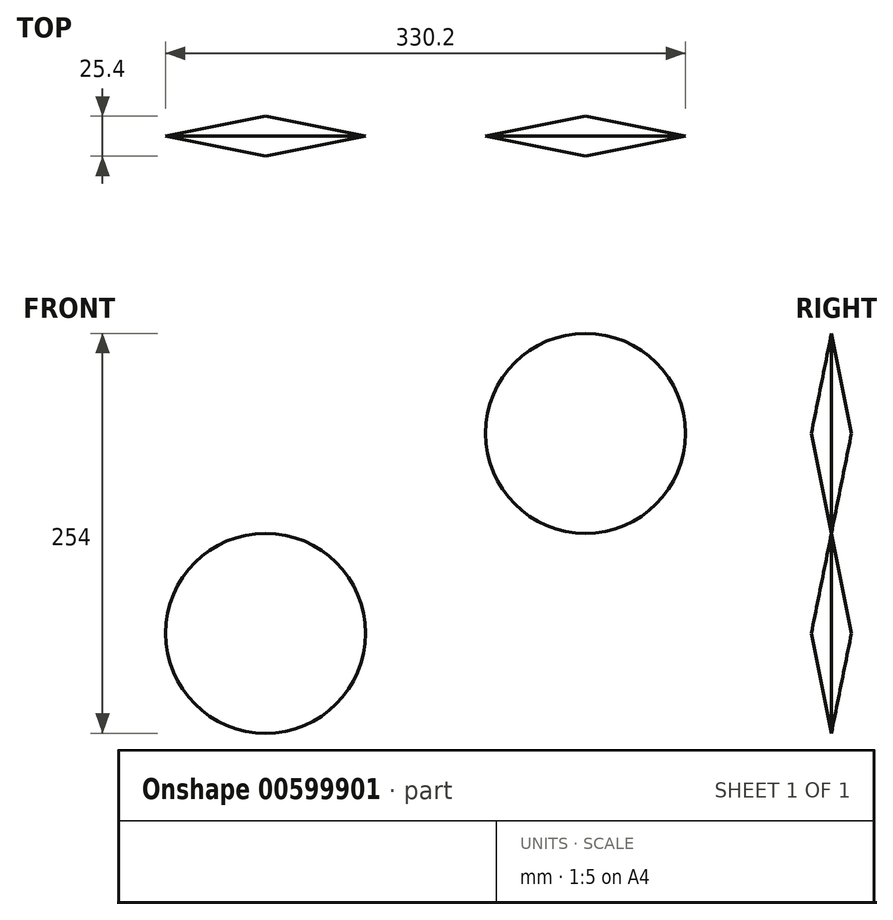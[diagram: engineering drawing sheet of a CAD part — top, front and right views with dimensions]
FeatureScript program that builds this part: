
annotation { "Feature Type Name" : "Feature", "Feature Type Description" : "" }
export const myFeature = defineFeature(function(context is Context, id is Id, definition is map)
    precondition{}
    {
        {
            var Q0;
            Q0=qCreatedBy(makeId("Front.planeOp"),FACE);
            var sketch = newSketch(context, id + "F0", { "sketchPlane" : qUnion([Q0])});
            skCircle(sketch, "E0", {"center": v(0, 0) * mm, "radius": 63.5 * mm});
            skSolve(sketch);
        }
        {
            var Q0;
            Q0 = qSketchRegion(id + "F0", true);
            extrude(context, id + "F1", {"entities" : qUnion([Q0]), "depth" : 25.4 * mm, "offsetDistance" : 25.4 * mm});
        }
        {
            var Q0;
            Q0=qCreatedBy(makeId("Top.planeOp"),FACE);
            var sketch = newSketch(context, id + "F2", { "sketchPlane" : qUnion([Q0])});
            skLineSegment(sketch, "E1", {"start": v(63.5, 0) * mm, "end": v(63.5, -25.4) * mm});
            skLineSegment(sketch, "E2.0", {"start": v(63.5, -25.4) * mm, "end": v(-63.5, -25.4) * mm});
            skLineSegment(sketch, "E3.0", {"start": v(63.5, 0) * mm, "end": v(-63.5, 0) * mm});
            skLineSegment(sketch, "E4", {"start": v(63.5, -12.7) * mm, "end": v(0, -25.4) * mm});
            skLineSegment(sketch, "E5", {"start": v(0, -25.4) * mm, "end": v(63.5, -25.4) * mm});
            skLineSegment(sketch, "E6", {"start": v(63.5, -12.7) * mm, "end": v(0, 0) * mm});
            skLineSegment(sketch, "E7", {"start": v(0, 0) * mm, "end": v(63.5, 0) * mm});
            skSolve(sketch);
        }
        {
            var Q0;
            Q0=qCreatedBy(makeId("Top.planeOp"),FACE);
            var sketch = newSketch(context, id + "F3", { "sketchPlane" : qUnion([Q0])});
            skLineSegment(sketch, "E8", {"start": v(0, 0) * mm, "end": v(0, 42.85) * mm});
            skSolve(sketch);
        }
        {
            var Q0;
            {var subQ2=sQuery(id+"F2.wireOp",EDGE,"E4");Q0=makeQuery(id+"F2.imprint","IMPRINT",FACE,{"disambiguationData":[TD([[makeQuery(id+"F2.imprint","IMPRINT",EDGE,{"derivedFrom":subQ2}),1.0]])]});}
            var Q1;
            {var subQ2=sQuery(id+"F2.wireOp",EDGE,"E6");Q1=makeQuery(id+"F2.imprint","IMPRINT",FACE,{"disambiguationData":[TD([[makeQuery(id+"F2.imprint","IMPRINT",EDGE,{"derivedFrom":subQ2}),-1.0]])]});}
            var Q2;
            Q2=sQuery(id+"F3.wireOp",EDGE,"E8");
            revolve(context, id + "F4", {"operationType" : NewBodyOperationType.REMOVE, "entities" : qUnion([Q0, Q1]), "axis" : qUnion([Q2]), "revolveType" : RevolveType.ONE_DIRECTION, "oppositeDirection" : true, "angle" : 350 * degree});
        }
        {
            var Q0;
            Q0=makeQuery(id+"F4.boolean.opBoolean","COPY",FACE,{"derivedFrom":makeQuery(id+"F4.opRevolve","CAP_FACE",FACE,{"disambiguationData":[OSD([sQuery(id+"F2.wireOp",EDGE,"E1"),sQuery(id+"F2.wireOp",EDGE,"E6"),sQuery(id+"F2.wireOp",EDGE,"E7")])],"isStart":true})});
            var sketch = newSketch(context, id + "F5", { "sketchPlane" : qUnion([Q0])});
            skLineSegment(sketch, "E9.0.0", {"start": v(0, 0) * mm, "end": v(63.5, -12.7) * mm});
            skLineSegment(sketch, "E9.0.1", {"start": v(63.5, -12.7) * mm, "end": v(63.5, 0) * mm});
            skLineSegment(sketch, "E9.0.2", {"start": v(63.5, 0) * mm, "end": v(0, 0) * mm});
            skLineSegment(sketch, "E10.0.0", {"start": v(63.5, -25.4) * mm, "end": v(63.5, -12.7) * mm});
            skLineSegment(sketch, "E10.0.1", {"start": v(63.5, -12.7) * mm, "end": v(0, -25.4) * mm});
            skLineSegment(sketch, "E10.0.2", {"start": v(0, -25.4) * mm, "end": v(63.5, -25.4) * mm});
            skSolve(sketch);
        }
        {
            var Q0;
            Q0 = qSketchRegion(id + "F5", true);
            var Q1;
            Q1=sQuery(id+"F3.wireOp",EDGE,"E8");
            revolve(context, id + "F6", {"operationType" : NewBodyOperationType.REMOVE, "entities" : qUnion([Q0]), "axis" : qUnion([Q1]), "revolveType" : RevolveType.ONE_DIRECTION, "angle" : 30 * degree});
        }
        {
            var Q0;
            Q0=makeQuery(id+"F1.opExtrude","SWEPT_BODY",BODY,{"disambiguationData":[OSD([sQuery(id+"F0.wireOp",EDGE,"E0")])]});
            transform(context, id + "F7", {"entities" : qUnion([Q0]), "transformType" : TransformType.TRANSLATION_3D, "dx" : 0 * mm, "dy" : 0 * mm, "dz" : 0 * mm, "makeCopy" : true});
        }
        {
            var Q0;
            Q0=makeQuery(id+"F7.opPattern","COPY",BODY,{"derivedFrom":makeQuery(id+"F1.opExtrude","SWEPT_BODY",BODY,{"disambiguationData":[OSD([sQuery(id+"F0.wireOp",EDGE,"E0")])]}),"instanceName":"1"});
            transform(context, id + "F8", {"entities" : qUnion([Q0]), "transformType" : TransformType.TRANSLATION_3D, "dx" : 203.2 * mm, "dy" : 0 * mm, "dz" : 127 * mm, "makeCopy" : false});
        }
    });
